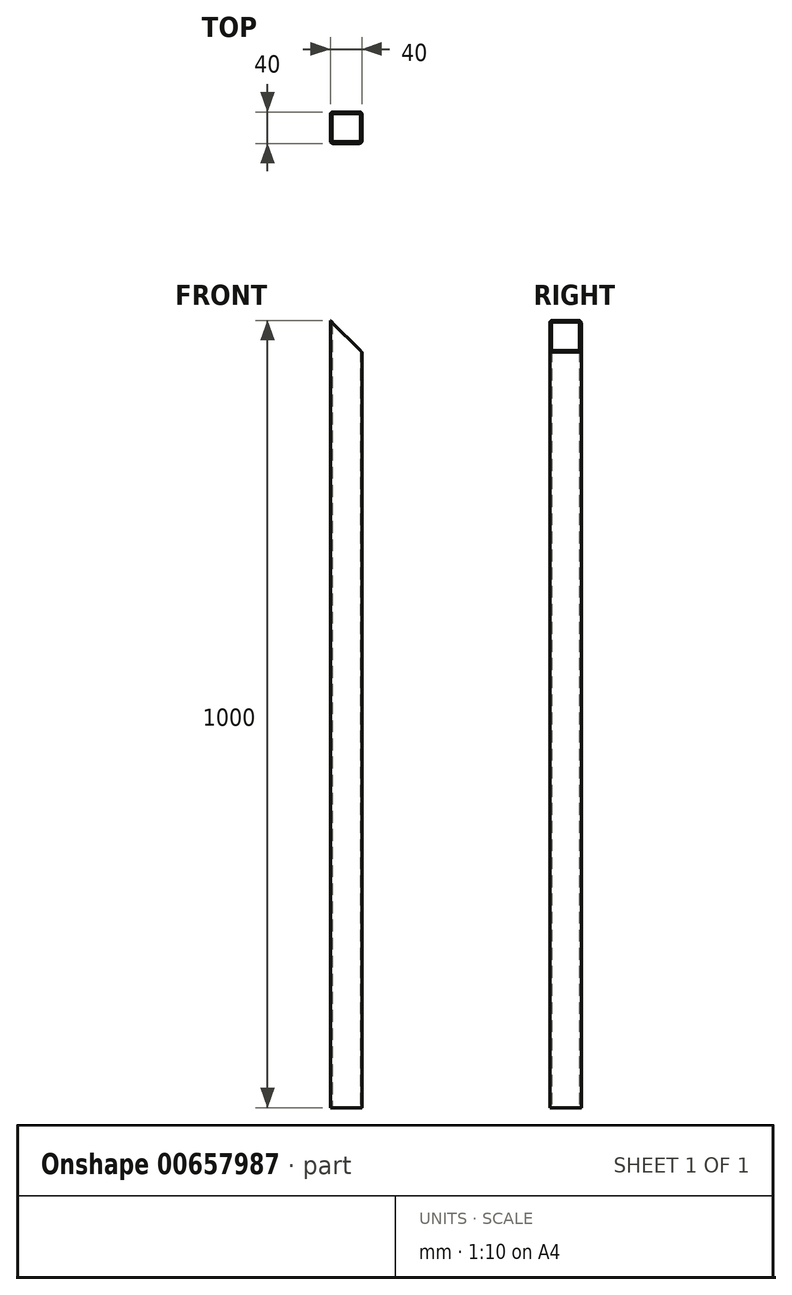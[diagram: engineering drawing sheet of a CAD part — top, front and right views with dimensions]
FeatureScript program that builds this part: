
annotation { "Feature Type Name" : "Feature", "Feature Type Description" : "" }
export const myFeature = defineFeature(function(context is Context, id is Id, definition is map)
    precondition{}
    {
        {
            var Q0;
            Q0=qCreatedBy(makeId("Top.planeOp"),FACE);
            var sketch = newSketch(context, id + "F0", { "sketchPlane" : qUnion([Q0])});
            skLineSegment(sketch, "E0.bottom", {"start": v(-17, 20) * mm, "end": v(17, 20) * mm});
            skLineSegment(sketch, "E0.top", {"start": v(-17, -20) * mm, "end": v(17, -20) * mm});
            skLineSegment(sketch, "E0.left", {"start": v(-20, 17) * mm, "end": v(-20, -17) * mm});
            skLineSegment(sketch, "E0.right", {"start": v(20, 17) * mm, "end": v(20, -17) * mm});
            skPoint(sketch, "E0.middle", {"position": v(0, 0) * mm});
            skPoint(sketch, "E1.visualSharp", {"position": v(-20, 20) * mm});
            skArc(sketch, "E1.filletArc", {"start": v(-17, 20) * mm, "mid": v(-19.12, 19.12) * mm, "end": v(-20, 17) * mm});
            skPoint(sketch, "E2.visualSharp", {"position": v(20, 20) * mm});
            skArc(sketch, "E2.filletArc", {"start": v(20, 17) * mm, "mid": v(19.12, 19.12) * mm, "end": v(17, 20) * mm});
            skPoint(sketch, "E3.visualSharp", {"position": v(20, -20) * mm});
            skArc(sketch, "E3.filletArc", {"start": v(17, -20) * mm, "mid": v(19.12, -19.12) * mm, "end": v(20, -17) * mm});
            skPoint(sketch, "E4.visualSharp", {"position": v(-20, -20) * mm});
            skArc(sketch, "E4.filletArc", {"start": v(-20, -17) * mm, "mid": v(-19.12, -19.12) * mm, "end": v(-17, -20) * mm});
            skLineSegment(sketch, "E5.0", {"start": v(-18, 18) * mm, "end": v(-18, -18) * mm});
            skLineSegment(sketch, "E5.1", {"start": v(-18, 18) * mm, "end": v(18, 18) * mm});
            skLineSegment(sketch, "E5.2", {"start": v(18, 18) * mm, "end": v(18, -18) * mm});
            skLineSegment(sketch, "E5.3", {"start": v(-18, -18) * mm, "end": v(18, -18) * mm});
            skSolve(sketch);
        }
        {
            var Q0;
            Q0=makeQuery(id+"F0.imprint","IMPRINT",FACE,{"disambiguationData":[TD([[makeQuery(id+"F0.imprint","IMPRINT",EDGE,{"derivedFrom":sQuery(id+"F0.wireOp",EDGE,"E0.bottom")}),-1.0]])]});
            extrude(context, id + "F1", {"entities" : qUnion([Q0]), "endBound" : BoundingType.SYMMETRIC, "depth" : 1000 * mm, "offsetDistance" : 25 * mm});
        }
        {
            var Q0;
            Q0=makeQuery(id+"F1.opExtrude","SWEPT_FACE",FACE,{"disambiguationData":[OSD([sQuery(id+"F0.wireOp",EDGE,"E0.top")])]});
            var sketch = newSketch(context, id + "F2", { "sketchPlane" : qUnion([Q0])});
            skLineSegment(sketch, "E6.0", {"start": v(-20, 500) * mm, "end": v(-20, -500) * mm, "construction": true});
            skLineSegment(sketch, "E7", {"start": v(-20, 500) * mm, "end": v(20, 500) * mm});
            skLineSegment(sketch, "E8", {"start": v(-20, 500) * mm, "end": v(20, 460) * mm});
            skPoint(sketch, "E9.orphan", {"position": v(20, -500) * mm});
            skLineSegment(sketch, "E10", {"start": v(20, 500) * mm, "end": v(20, 460) * mm});
            skSolve(sketch);
        }
        {
            var Q0;
            Q0=qSketchRegion(id+"F2",true);
            extrude(context, id + "F3", {"entities" : qUnion([Q0]), "operationType" : NewBodyOperationType.REMOVE, "endBound" : BoundingType.THROUGH_ALL, "oppositeDirection" : true, "depth" : 25 * mm, "offsetDistance" : 25 * mm});
        }
    });
